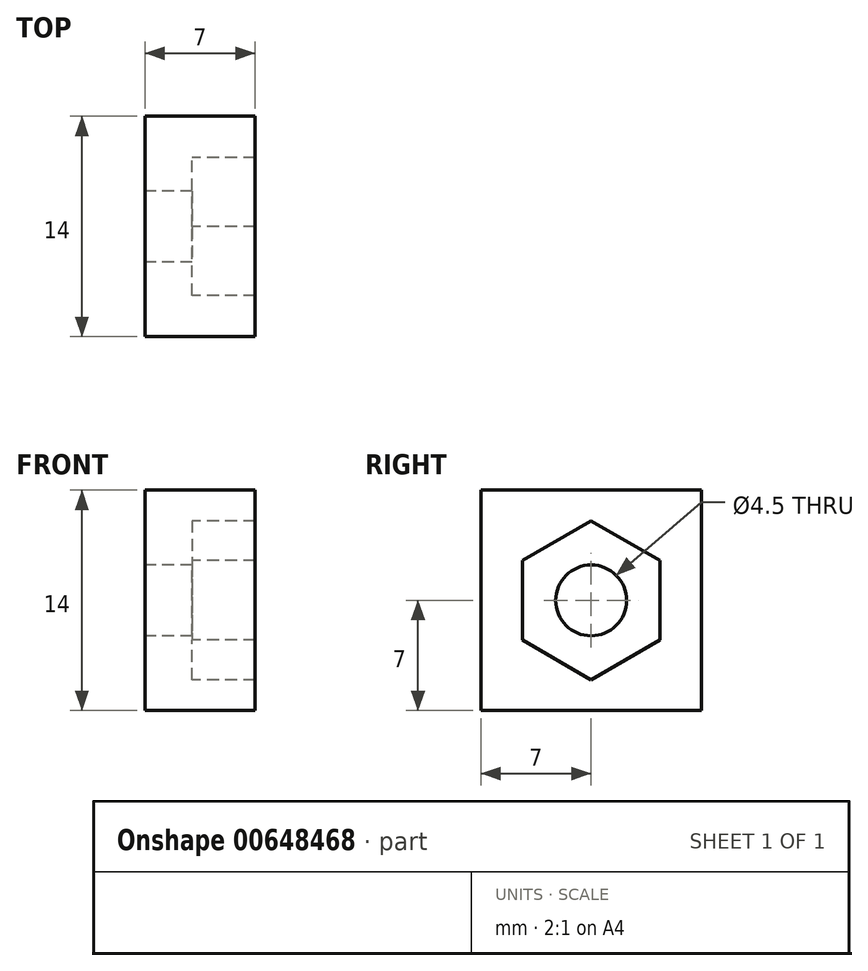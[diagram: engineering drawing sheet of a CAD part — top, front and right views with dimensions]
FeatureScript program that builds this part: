
annotation { "Feature Type Name" : "Feature", "Feature Type Description" : "" }
export const myFeature = defineFeature(function(context is Context, id is Id, definition is map)
    precondition{}
    {
        {
            var Q0;
            Q0=qCreatedBy(makeId("Top.planeOp"),FACE);
            var sketch = newSketch(context, id + "F0", { "sketchPlane" : qUnion([Q0])});
            skCircle(sketch, "E0", {"center": v(0, 0) * mm, "radius": 2.25 * mm});
            skLineSegment(sketch, "E1.bottom", {"start": v(7, 7) * mm, "end": v(-7, 7) * mm});
            skLineSegment(sketch, "E1.top", {"start": v(7, -7) * mm, "end": v(-7, -7) * mm});
            skLineSegment(sketch, "E1.left", {"start": v(7, 7) * mm, "end": v(7, -7) * mm});
            skLineSegment(sketch, "E1.right", {"start": v(-7, 7) * mm, "end": v(-7, -7) * mm});
            skCircle(sketch, "E2.cCircle", {"center": v(0, 0) * mm, "radius": 2.25 * mm, "construction": true});
            skLineSegment(sketch, "E2.1", {"start": v(1.95, 1.12) * mm, "end": v(1.95, -1.13) * mm});
            skSolve(sketch);
        }
        {
            var Q0;
            Q0=makeQuery(id+"F0.imprint","IMPRINT",FACE,{"disambiguationData":[TD([[makeQuery(id+"F0.imprint","IMPRINT",EDGE,{"derivedFrom":sQuery(id+"F0.wireOp",EDGE,"E1.bottom")}),1.0]])]});
            var Q1;
            {var subQ0=sQuery(id+"F0.wireOp",EDGE,"E2.3");Q1=makeQuery(id+"F0.imprint","IMPRINT",FACE,{"disambiguationData":[TD([[makeQuery(id+"F0.imprint","IMPRINT",EDGE,{"derivedFrom":subQ0}),1.0]])]});}
            var Q2;
            {var subQ0=sQuery(id+"F0.wireOp",EDGE,"E2.4");Q2=makeQuery(id+"F0.imprint","IMPRINT",FACE,{"disambiguationData":[TD([[makeQuery(id+"F0.imprint","IMPRINT",EDGE,{"derivedFrom":subQ0}),1.0]])]});}
            var Q3;
            {var subQ0=sQuery(id+"F0.wireOp",EDGE,"E2.5");Q3=makeQuery(id+"F0.imprint","IMPRINT",FACE,{"disambiguationData":[TD([[makeQuery(id+"F0.imprint","IMPRINT",EDGE,{"derivedFrom":subQ0}),1.0]])]});}
            var Q4;
            {var subQ0=sQuery(id+"F0.wireOp",EDGE,"E2.0");Q4=makeQuery(id+"F0.imprint","IMPRINT",FACE,{"disambiguationData":[TD([[makeQuery(id+"F0.imprint","IMPRINT",EDGE,{"derivedFrom":subQ0}),1.0]])]});}
            var Q5;
            {var subQ0=sQuery(id+"F0.wireOp",EDGE,"E2.2");Q5=makeQuery(id+"F0.imprint","IMPRINT",FACE,{"disambiguationData":[TD([[makeQuery(id+"F0.imprint","IMPRINT",EDGE,{"derivedFrom":subQ0}),1.0]])]});}
            extrude(context, id + "F1", {"entities" : qUnion([Q0, Q1, Q2, Q3, Q4, Q5]), "depth" : 3 * mm, "offsetDistance" : 25 * mm});
        }
        {
            var Q0;
            Q0=makeQuery(id+"F1.opExtrude","CAP_FACE",FACE,{"disambiguationData":[OSD([sQuery(id+"F0.wireOp",EDGE,"E0"),sQuery(id+"F0.wireOp",EDGE,"E1.bottom"),sQuery(id+"F0.wireOp",EDGE,"E1.top"),sQuery(id+"F0.wireOp",EDGE,"E1.left"),sQuery(id+"F0.wireOp",EDGE,"E1.right")])],"isStart":false});
            var sketch = newSketch(context, id + "F2", { "sketchPlane" : qUnion([Q0])});
            skPoint(sketch, "E3.0", {"position": v(0, 0) * mm});
            skCircle(sketch, "E4", {"center": v(0, 0) * mm, "radius": 5.05 * mm});
            skLineSegment(sketch, "E5.bottom", {"start": v(7, 7) * mm, "end": v(-7, 7) * mm});
            skLineSegment(sketch, "E5.top", {"start": v(7, -7) * mm, "end": v(-7, -7) * mm});
            skLineSegment(sketch, "E5.left", {"start": v(7, 7) * mm, "end": v(7, -7) * mm});
            skLineSegment(sketch, "E5.right", {"start": v(-7, 7) * mm, "end": v(-7, -7) * mm});
            skCircle(sketch, "E6.cCircle", {"center": v(0, 0) * mm, "radius": 5.05 * mm, "construction": true});
            skLineSegment(sketch, "E6.0", {"start": v(0, 5.05) * mm, "end": v(4.37, 2.52) * mm});
            skLineSegment(sketch, "E6.1", {"start": v(4.37, 2.52) * mm, "end": v(4.37, -2.53) * mm});
            skLineSegment(sketch, "E6.2", {"start": v(4.37, -2.53) * mm, "end": v(0, -5.05) * mm});
            skLineSegment(sketch, "E6.3", {"start": v(0, -5.05) * mm, "end": v(-4.37, -2.52) * mm});
            skLineSegment(sketch, "E6.4", {"start": v(-4.37, -2.52) * mm, "end": v(-4.37, 2.53) * mm});
            skLineSegment(sketch, "E6.5", {"start": v(-4.37, 2.53) * mm, "end": v(0, 5.05) * mm});
            skSolve(sketch);
        }
        {
            var Q0;
            Q0=makeQuery(id+"F2.imprint","IMPRINT",FACE,{"disambiguationData":[TD([[makeQuery(id+"F2.imprint","IMPRINT",EDGE,{"derivedFrom":sQuery(id+"F2.wireOp",EDGE,"E4")}),-1.0]])]});
            var Q1;
            {var subQ0=sQuery(id+"F2.wireOp",EDGE,"E6.4");Q1=makeQuery(id+"F2.imprint","IMPRINT",FACE,{"disambiguationData":[TD([[makeQuery(id+"F2.imprint","IMPRINT",EDGE,{"derivedFrom":subQ0}),1.0]])]});}
            var Q2;
            {var subQ0=sQuery(id+"F2.wireOp",EDGE,"E6.5");Q2=makeQuery(id+"F2.imprint","IMPRINT",FACE,{"disambiguationData":[TD([[makeQuery(id+"F2.imprint","IMPRINT",EDGE,{"derivedFrom":subQ0}),1.0]])]});}
            var Q3;
            {var subQ0=sQuery(id+"F2.wireOp",EDGE,"E6.0");Q3=makeQuery(id+"F2.imprint","IMPRINT",FACE,{"disambiguationData":[TD([[makeQuery(id+"F2.imprint","IMPRINT",EDGE,{"derivedFrom":subQ0}),1.0]])]});}
            var Q4;
            {var subQ0=sQuery(id+"F2.wireOp",EDGE,"E6.1");Q4=makeQuery(id+"F2.imprint","IMPRINT",FACE,{"disambiguationData":[TD([[makeQuery(id+"F2.imprint","IMPRINT",EDGE,{"derivedFrom":subQ0}),1.0]])]});}
            var Q5;
            {var subQ0=sQuery(id+"F2.wireOp",EDGE,"E6.2");Q5=makeQuery(id+"F2.imprint","IMPRINT",FACE,{"disambiguationData":[TD([[makeQuery(id+"F2.imprint","IMPRINT",EDGE,{"derivedFrom":subQ0}),1.0]])]});}
            var Q6;
            {var subQ0=sQuery(id+"F2.wireOp",EDGE,"E6.3");Q6=makeQuery(id+"F2.imprint","IMPRINT",FACE,{"disambiguationData":[TD([[makeQuery(id+"F2.imprint","IMPRINT",EDGE,{"derivedFrom":subQ0}),1.0]])]});}
            extrude(context, id + "F3", {"entities" : qUnion([Q0, Q1, Q2, Q3, Q4, Q5, Q6]), "operationType" : NewBodyOperationType.ADD, "depth" : 4 * mm, "offsetDistance" : 25 * mm});
        }
        {
            var Q0;
            Q0=makeQuery(id+"F1.opExtrude","SWEPT_BODY",BODY,{"disambiguationData":[OSD([sQuery(id+"F0.wireOp",EDGE,"E1.bottom"),sQuery(id+"F0.wireOp",EDGE,"E1.top"),sQuery(id+"F0.wireOp",EDGE,"E1.left"),sQuery(id+"F0.wireOp",EDGE,"E1.right"),sQuery(id+"F0.wireOp",EDGE,"E2.0"),sQuery(id+"F0.wireOp",EDGE,"E2.1"),sQuery(id+"F0.wireOp",EDGE,"E2.2"),sQuery(id+"F0.wireOp",EDGE,"E2.3"),sQuery(id+"F0.wireOp",EDGE,"E2.4"),sQuery(id+"F0.wireOp",EDGE,"E2.5")])]});
            var Q1;
            Q1=makeQuery(id+"F1.opExtrude","CAP_EDGE",EDGE,{"disambiguationData":[OSD([sQuery(id+"F0.wireOp",EDGE,"E1.top")])],"isStart":true});
            transform(context, id + "F4", {"entities" : qUnion([Q0]), "transformType" : TransformType.ROTATION, "transformAxis" : qUnion([Q1]), "angle" : 90 * degree, "oppositeDirection" : true, "makeCopy" : false});
        }
        {
            var Q0;
            Q0=makeQuery(id+"F1.opExtrude","SWEPT_BODY",BODY,{"disambiguationData":[OSD([sQuery(id+"F0.wireOp",EDGE,"E1.bottom"),sQuery(id+"F0.wireOp",EDGE,"E1.top"),sQuery(id+"F0.wireOp",EDGE,"E1.left"),sQuery(id+"F0.wireOp",EDGE,"E1.right"),sQuery(id+"F0.wireOp",EDGE,"E2.0"),sQuery(id+"F0.wireOp",EDGE,"E2.1"),sQuery(id+"F0.wireOp",EDGE,"E2.2"),sQuery(id+"F0.wireOp",EDGE,"E2.3"),sQuery(id+"F0.wireOp",EDGE,"E2.4"),sQuery(id+"F0.wireOp",EDGE,"E2.5")])]});
            var Q1;
            Q1=makeQuery(id+"F1.opExtrude","CAP_EDGE",EDGE,{"disambiguationData":[OSD([sQuery(id+"F0.wireOp",EDGE,"E1.left")])],"isStart":true});
            transform(context, id + "F5", {"entities" : qUnion([Q0]), "transformType" : TransformType.ROTATION, "transformAxis" : qUnion([Q1]), "angle" : 90 * degree, "oppositeDirection" : true, "makeCopy" : false});
        }
    });
